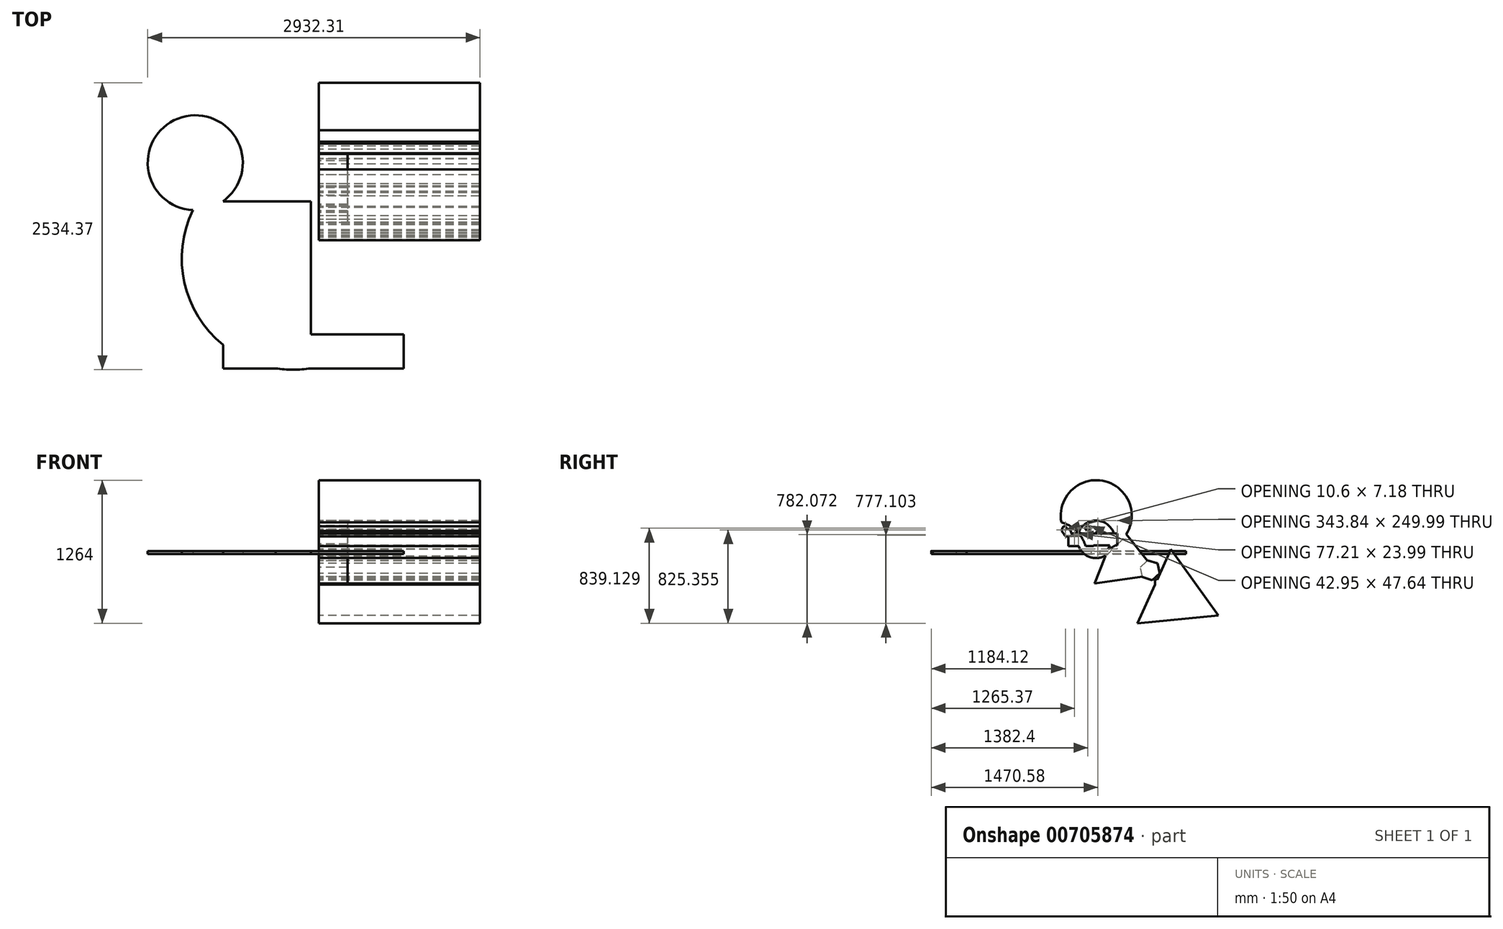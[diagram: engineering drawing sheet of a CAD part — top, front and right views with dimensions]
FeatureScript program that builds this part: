
annotation { "Feature Type Name" : "Feature", "Feature Type Description" : "" }
export const myFeature = defineFeature(function(context is Context, id is Id, definition is map)
    precondition{}
    {
        {
            var Q0;
            Q0=qCreatedBy(makeId("Right.planeOp"),FACE);
            var sketch = newSketch(context, id + "F0", { "sketchPlane" : qUnion([Q0])});
            skLineSegment(sketch, "E0", {"start": v(-335.18, 198.14) * mm, "end": v(-190.43, 140.4) * mm});
            skLineSegment(sketch, "E1", {"start": v(-190.43, 140.4) * mm, "end": v(-234.76, 86.82) * mm});
            skLineSegment(sketch, "E2", {"start": v(-234.76, 86.82) * mm, "end": v(-335.18, 198.14) * mm});
            skFitSpline(sketch, "E3", {"points": [v(-272.76, 165.37) * mm, v(-238.38, 145.04) * mm, v(-228.43, 122.3) * mm, v(-272.76, 165.37) * mm]});
            skLineSegment(sketch, "E4", {"start": v(-238.38, 145.04) * mm, "end": v(-233.4, 157.54) * mm});
            skLineSegment(sketch, "E5", {"start": v(-224.8, 132) * mm, "end": v(-204.2, 123.77) * mm});
            skLineSegment(sketch, "E6", {"start": v(-224.8, 132) * mm, "end": v(-224.8, 145.04) * mm});
            skLineSegment(sketch, "E7", {"start": v(-206.72, 138.1) * mm, "end": v(-238.38, 150.72) * mm});
            skFitSpline(sketch, "E8", {"points": [v(-293.75, 171.25) * mm, v(-290.19, 158.66) * mm, v(-249.17, 123.74) * mm, v(-293.75, 171.25) * mm]});
            skPoint(sketch, "E9", {"position": v(-252.74, 145.04) * mm});
            skArc(sketch, "E10", {"start": v(-273.24, 78.11) * mm, "mid": v(-320.98, 158.46) * mm, "end": v(-410.57, 131.84) * mm});
            skArc(sketch, "E11", {"start": v(-312.17, 154.35) * mm, "mid": v(-388.8, 152.96) * mm, "end": v(-348.69, 87.65) * mm});
            skPoint(sketch, "E12", {"position": v(-312.17, 115.96) * mm});
            skPoint(sketch, "E13", {"position": v(-333.88, 115.96) * mm});
            skPoint(sketch, "E14", {"position": v(-337.45, 144.7) * mm});
            skPoint(sketch, "E15", {"position": v(-366.87, 144.7) * mm});
            skPoint(sketch, "E16", {"position": v(-372.22, 129.15) * mm});
            skPoint(sketch, "E17", {"position": v(-321.4, 90.35) * mm});
            skPoint(sketch, "E18", {"position": v(-337.45, 133.14) * mm});
            skPoint(sketch, "E19", {"position": v(-345.47, 144.7) * mm});
            skPoint(sketch, "E20", {"position": v(-262.54, 103.65) * mm});
            skPoint(sketch, "E21", {"position": v(-238.38, 105.65) * mm});
            skCircle(sketch, "E22", {"center": v(-234.01, 227.87) * mm, "radius": 21.9 * mm});
            skCircle(sketch, "E23", {"center": v(-221.2, 210.1) * mm, "radius": 8.15 * mm});
            skCircle(sketch, "E24", {"center": v(-158.22, 185.34) * mm, "radius": 5.27 * mm});
            skCircle(sketch, "E25", {"center": v(-160.9, 127.99) * mm, "radius": 165.89 * mm});
            skCircle(sketch, "E26.cCircle", {"center": v(-437.32, 208.54) * mm, "radius": 25.56 * mm, "construction": true});
            skLineSegment(sketch, "E26.0", {"start": v(-428.22, 236.62) * mm, "end": v(-408.45, 214.7) * mm});
            skLineSegment(sketch, "E26.1", {"start": v(-408.45, 214.7) * mm, "end": v(-417.54, 186.62) * mm});
            skLineSegment(sketch, "E26.2", {"start": v(-417.54, 186.62) * mm, "end": v(-446.41, 180.46) * mm});
            skLineSegment(sketch, "E26.3", {"start": v(-446.41, 180.46) * mm, "end": v(-466.18, 202.38) * mm});
            skLineSegment(sketch, "E26.4", {"start": v(-466.18, 202.38) * mm, "end": v(-457.09, 230.46) * mm});
            skLineSegment(sketch, "E26.5", {"start": v(-457.09, 230.46) * mm, "end": v(-428.22, 236.62) * mm});
            skPoint(sketch, "E26.0.midPoint", {"position": v(-418.33, 225.67) * mm});
            skCircle(sketch, "E27.cCircle", {"center": v(314.38, -145.17) * mm, "radius": 77.54 * mm, "construction": true});
            skLineSegment(sketch, "E27.0", {"start": v(399.56, -172.76) * mm, "end": v(333.08, -232.73) * mm});
            skLineSegment(sketch, "E27.1", {"start": v(333.08, -232.73) * mm, "end": v(247.9, -205.14) * mm});
            skLineSegment(sketch, "E27.2", {"start": v(247.9, -205.14) * mm, "end": v(229.2, -117.58) * mm});
            skLineSegment(sketch, "E27.3", {"start": v(229.2, -117.58) * mm, "end": v(295.68, -57.6) * mm});
            skLineSegment(sketch, "E27.4", {"start": v(295.68, -57.6) * mm, "end": v(380.86, -85.2) * mm});
            skLineSegment(sketch, "E27.5", {"start": v(380.86, -85.2) * mm, "end": v(399.56, -172.76) * mm});
            skPoint(sketch, "E27.0.midPoint", {"position": v(366.32, -202.75) * mm});
            skCircle(sketch, "E28.cCircle", {"center": v(395.52, -281.5) * mm, "radius": 36.56 * mm, "construction": true});
            skLineSegment(sketch, "E28.0", {"start": v(358.96, -344.82) * mm, "end": v(358.96, -218.17) * mm});
            skLineSegment(sketch, "E28.1", {"start": v(358.96, -218.17) * mm, "end": v(468.64, -281.5) * mm});
            skLineSegment(sketch, "E28.2", {"start": v(468.64, -281.5) * mm, "end": v(358.96, -344.82) * mm});
            skPoint(sketch, "E28.0.midPoint", {"position": v(358.96, -281.5) * mm});
            skCircle(sketch, "E29.cCircle", {"center": v(82.54, -60.65) * mm, "radius": 163.68 * mm, "construction": true});
            skLineSegment(sketch, "E29.0", {"start": v(-174.54, -263.31) * mm, "end": v(35.57, 263.31) * mm});
            skLineSegment(sketch, "E29.1", {"start": v(35.57, 263.31) * mm, "end": v(386.59, -181.96) * mm});
            skLineSegment(sketch, "E29.2", {"start": v(386.59, -181.96) * mm, "end": v(-174.54, -263.31) * mm});
            skPoint(sketch, "E29.0.midPoint", {"position": v(-69.48, 0) * mm});
            skCircle(sketch, "E30.cCircle", {"center": v(540.51, -371.93) * mm, "radius": 207.44 * mm, "construction": true});
            skLineSegment(sketch, "E30.0", {"start": v(203.01, -613.22) * mm, "end": v(500.3, 41) * mm});
            skLineSegment(sketch, "E30.1", {"start": v(500.3, 41) * mm, "end": v(918.23, -543.57) * mm});
            skLineSegment(sketch, "E30.2", {"start": v(918.23, -543.57) * mm, "end": v(203.01, -613.22) * mm});
            skPoint(sketch, "E30.0.midPoint", {"position": v(351.66, -286.11) * mm});
            skArc(sketch, "E31", {"start": v(-247.39, 37.9) * mm, "mid": v(-321.76, 190.14) * mm, "end": v(-466.74, 277.83) * mm});
            skArc(sketch, "E32", {"start": v(-249.17, 37.9) * mm, "mid": v(72.3, 548.04) * mm, "end": v(-466.74, 277.83) * mm});
            skArc(sketch, "E33", {"start": v(-437.32, 208.54) * mm, "mid": v(-428.22, 236.62) * mm, "end": v(-457.09, 230.46) * mm});
            skArc(sketch, "E34", {"start": v(-446.41, 180.46) * mm, "mid": v(-382.68, 175.33) * mm, "end": v(-437.32, 208.54) * mm});
            skLineSegment(sketch, "E35.bottom", {"start": v(-406.1, 178.52) * mm, "end": v(-183.18, 178.52) * mm});
            skLineSegment(sketch, "E35.top", {"start": v(-406.1, 69.64) * mm, "end": v(-183.18, 69.64) * mm});
            skLineSegment(sketch, "E35.left", {"start": v(-406.1, 178.52) * mm, "end": v(-406.1, 69.64) * mm});
            skLineSegment(sketch, "E35.right", {"start": v(-183.18, 178.52) * mm, "end": v(-183.18, 69.64) * mm});
            skLineSegment(sketch, "E36.bottom", {"start": v(-183.18, 178.52) * mm, "end": v(26.36, 178.52) * mm});
            skLineSegment(sketch, "E36.top", {"start": v(-183.18, 73.49) * mm, "end": v(26.36, 73.49) * mm});
            skLineSegment(sketch, "E36.left", {"start": v(-183.18, 178.52) * mm, "end": v(-183.18, 73.49) * mm});
            skLineSegment(sketch, "E36.right", {"start": v(26.36, 178.52) * mm, "end": v(26.36, 73.49) * mm});
            skSolve(sketch);
        }
        {
            var Q0;
            Q0=makeQuery(id+"F0.imprint","IMPRINT",FACE,{"disambiguationData":[TD([[makeQuery(id+"F0.imprint","IMPRINT",EDGE,{"derivedFrom":sQuery(id+"F0.wireOp",EDGE,"E24")}),-1.0]])]});
            var Q1;
            {var subQ10=sQuery(id+"F0.wireOp",EDGE,"E29.0");var subQ12=sQuery(id+"F0.wireOp",EDGE,"E25");var subQ13=makeQuery(id+"F0.imprint","INTERSECT",VERTEX,{"disambiguationData":[OD(0.0)],"derivedFrom":[subQ12,subQ10]});Q1=makeQuery(id+"F0.imprint","IMPRINT",FACE,{"disambiguationData":[TD([[makeQuery(id+"F0.imprint","IMPRINT",EDGE,{"disambiguationData":[TD([[subQ13,-1.0]])],"derivedFrom":subQ12}),-1.0]])]});}
            extrude(context, id + "F1", {"entities" : qUnion([Q0, Q1]), "depth" : 254 * mm, "offsetDistance" : 25.4 * mm});
        }
        {
            var Q0;
            Q0 = qSketchRegion(id + "F0", true);
            extrude(context, id + "F2", {"entities" : qUnion([Q0]), "depth" : 1422.4 * mm, "offsetDistance" : 25.4 * mm});
        }
        {
            var Q0;
            Q0=qCreatedBy(makeId("Top.planeOp"),FACE);
            var sketch = newSketch(context, id + "F3", { "sketchPlane" : qUnion([Q0])});
            skArc(sketch, "E37", {"start": v(-1111.75, -206.35) * mm, "mid": v(-1014.66, -1220.21) * mm, "end": v(-71.16, -1603.84) * mm});
            skArc(sketch, "E38", {"start": v(-1068.9, -206.35) * mm, "mid": v(-1090.32, 632.27) * mm, "end": v(-1111.75, -206.35) * mm});
            skLineSegment(sketch, "E39.bottom", {"start": v(-71.16, -1603.84) * mm, "end": v(-845.82, -1603.84) * mm});
            skLineSegment(sketch, "E39.top", {"start": v(-71.16, -128.3) * mm, "end": v(-845.82, -128.3) * mm});
            skLineSegment(sketch, "E39.left", {"start": v(-71.16, -1603.84) * mm, "end": v(-71.16, -128.3) * mm});
            skLineSegment(sketch, "E39.right", {"start": v(-845.82, -1603.84) * mm, "end": v(-845.82, -128.3) * mm});
            skLineSegment(sketch, "E40.bottom", {"start": v(-71.16, -1603.84) * mm, "end": v(750.16, -1603.84) * mm});
            skLineSegment(sketch, "E40.top", {"start": v(-71.16, -1303.8) * mm, "end": v(750.16, -1303.8) * mm});
            skLineSegment(sketch, "E40.left", {"start": v(-71.16, -1603.84) * mm, "end": v(-71.16, -1303.8) * mm});
            skLineSegment(sketch, "E40.right", {"start": v(750.16, -1603.84) * mm, "end": v(750.16, -1303.8) * mm});
            skSolve(sketch);
        }
        {
            var Q0;
            {var subQ1=sQuery(id+"F3.wireOp",EDGE,"E39.top");var subQ4=sQuery(id+"F3.wireOp",EDGE,"E40.bottom");var subQ5=sQuery(id+"F3.wireOp",EDGE,"E39.bottom");var subQ6=sQuery(id+"F3.wireOp",EDGE,"E37");var subQ8=makeQuery(id+"F3.imprint","INTERSECT",VERTEX,{"derivedFrom":[subQ6,subQ5]});var subQ12=makeQuery(id+"F3.imprint","IMPRINT",EDGE,{"disambiguationData":[TD([[subQ8,1.0]])],"derivedFrom":subQ6});var subQ14=sQuery(id+"F3.wireOp",EDGE,"E38");var subQ18=makeQuery(id+"F3.imprint","INTERSECT",VERTEX,{"derivedFrom":[subQ6,subQ14]});Q0=qUnion([makeQuery(id+"F3.imprint","IMPRINT",FACE,{"disambiguationData":[TD([[makeQuery(id+"F3.imprint","IMPRINT",EDGE,{"disambiguationData":[TD([[subQ18,-1.0]])],"derivedFrom":subQ6}),1.0]])]}),makeQuery(id+"F3.imprint","IMPRINT",FACE,{"disambiguationData":[TD([[subQ12,-1.0]])]}),makeQuery(id+"F3.imprint","IMPRINT",FACE,{"disambiguationData":[TD([[makeQuery(id+"F3.imprint","IMPRINT",EDGE,{"disambiguationData":[TD([[subQ8,-1.0]])],"derivedFrom":subQ6}),1.0]])]}),makeQuery(id+"F3.imprint","IMPRINT",FACE,{"disambiguationData":[TD([[makeQuery(id+"F3.imprint","IMPRINT",EDGE,{"derivedFrom":subQ4}),1.0]])]}),makeQuery(id+"F3.imprint","IMPRINT",FACE,{"disambiguationData":[TD([[makeQuery(id+"F3.imprint","IMPRINT",EDGE,{"derivedFrom":subQ1}),1.0]])]})]);}
            extrude(context, id + "F4", {"entities" : qUnion([Q0]), "depth" : 25.4 * mm, "offsetDistance" : 25.4 * mm});
        }
        {
            var Q0;
            {var subQ0=sQuery(id+"F0.wireOp",EDGE,"E25");Q0=makeQuery(id+"F2.opExtrude","SWEPT_FACE",FACE,{"disambiguationData":[OSD([subQ0]),TDD([makeQuery(id+"F0.imprint","IMPRINT",EDGE,{"disambiguationData":[TD([[makeQuery(id+"F0.imprint","INTERSECT",VERTEX,{"derivedFrom":[subQ0,sQuery(id+"F0.wireOp",EDGE,"E35.top")]}),-1.0]])],"derivedFrom":subQ0})])]});}
            fillet(context, id + "F5", {"entities" : qUnion([Q0]), "radius" : 5.08 * mm, "tangentPropagation" : true, "allowEdgeOverflow" : false});
        }
    });
